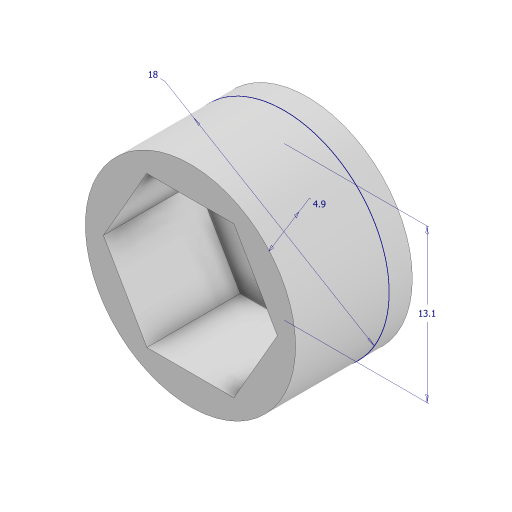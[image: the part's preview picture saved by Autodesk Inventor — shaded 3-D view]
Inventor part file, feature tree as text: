
AUTODESK INVENTOR PART (.ipt)
format: ipt  version: 2023 (Build 270158000, 158)  size: 127,488 bytes
history: native  units: mm
features: extrude x2, sketch x1
ambient origin geometry x8: Origin, YZ Plane, XZ Plane, XY Plane, X Axis, Y Axis, Z Axis, Center Point
bodies: Solid1 (feature_tree)
feature tree (3):
  sketch  "Sketch1"  dims[d0=13.1mm d1=18.0mm d2=4.9mm d3=8.0mm d4=0.0mm d5=2.0mm d6=0.0mm]
  extrude  "Extrusion1"  Depth=2.0mm
  extrude  "Extrusion2"  Depth=2.0mm
